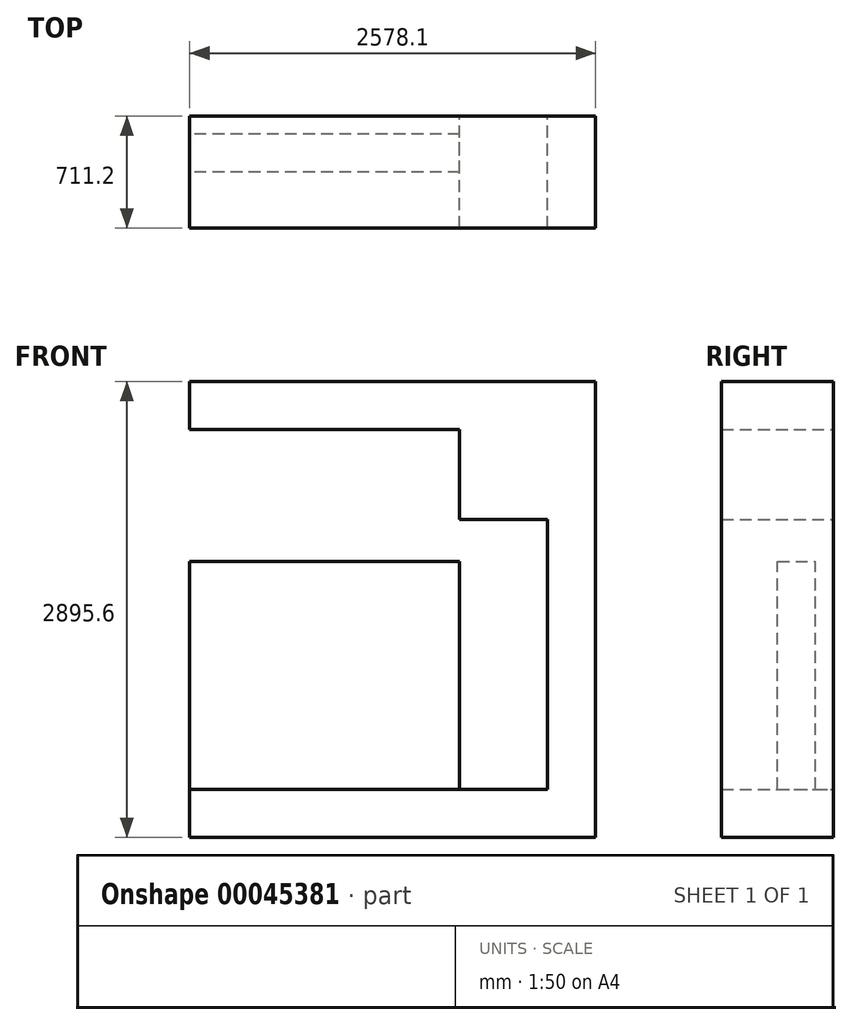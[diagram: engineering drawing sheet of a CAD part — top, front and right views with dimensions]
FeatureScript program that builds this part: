
annotation { "Feature Type Name" : "Feature", "Feature Type Description" : "" }
export const myFeature = defineFeature(function(context is Context, id is Id, definition is map)
    precondition{}
    {
        {
            var Q0;
            Q0=qCreatedBy(makeId("Front.planeOp"),FACE);
            var sketch = newSketch(context, id + "F0", { "sketchPlane" : qUnion([Q0])});
            skLineSegment(sketch, "E0", {"start": v(1136.65, 0) * mm, "end": v(-1136.65, 0) * mm});
            skPoint(sketch, "E1", {"position": v(0, 0) * mm});
            skLineSegment(sketch, "E2", {"start": v(1136.65, 0) * mm, "end": v(1136.65, 1714.5) * mm});
            skLineSegment(sketch, "E3", {"start": v(577.85, 2286) * mm, "end": v(-1136.65, 2286) * mm});
            skLineSegment(sketch, "E4", {"start": v(577.85, 1714.5) * mm, "end": v(577.85, 2286) * mm});
            skLineSegment(sketch, "E5", {"start": v(577.85, 1714.5) * mm, "end": v(1136.65, 1714.5) * mm});
            skLineSegment(sketch, "E6", {"start": v(-1136.65, 2286) * mm, "end": v(-1136.65, 2590.8) * mm});
            skLineSegment(sketch, "E7", {"start": v(-1136.65, 2590.8) * mm, "end": v(1441.45, 2590.8) * mm});
            skLineSegment(sketch, "E8", {"start": v(1441.45, 2590.8) * mm, "end": v(1441.45, -304.8) * mm});
            skLineSegment(sketch, "E9", {"start": v(1441.45, -304.8) * mm, "end": v(-1136.65, -304.8) * mm});
            skLineSegment(sketch, "E10", {"start": v(-1136.65, -304.8) * mm, "end": v(-1136.65, 0) * mm});
            skSolve(sketch);
        }
        {
            var Q0;
            Q0 = qSketchRegion(id + "F0", true);
            extrude(context, id + "F1", {"entities" : qUnion([Q0]), "endBound" : BoundingType.SYMMETRIC, "depth" : 711.2 * mm});
        }
        {
            var Q0;
            Q0=qCreatedBy(makeId("Front.planeOp"),FACE);
            var sketch = newSketch(context, id + "F2", { "sketchPlane" : qUnion([Q0])});
            skLineSegment(sketch, "E11", {"start": v(-1136.65, 0) * mm, "end": v(-1136.65, 1447.8) * mm});
            skLineSegment(sketch, "E12", {"start": v(-1136.65, 1447.8) * mm, "end": v(577.85, 1447.8) * mm});
            skLineSegment(sketch, "E13.0", {"start": v(577.85, 0) * mm, "end": v(-1136.65, 0) * mm});
            skLineSegment(sketch, "E14", {"start": v(577.85, 1714.5) * mm, "end": v(577.85, 0) * mm, "construction": true});
            skLineSegment(sketch, "E15", {"start": v(577.85, 0) * mm, "end": v(577.85, 1447.8) * mm});
            skSolve(sketch);
        }
        {
            var Q0;
            Q0 = qSketchRegion(id + "F2", true);
            extrude(context, id + "F3", {"entities" : qUnion([Q0]), "depth" : 28 / 50.8 * mm});
        }
        {
            var Q0;
            Q0=makeQuery(id+"F3.opExtrude","CAP_FACE",FACE,{"disambiguationData":[OSD([sQuery(id+"F2.wireOp",EDGE,"E11"),sQuery(id+"F2.wireOp",EDGE,"E12"),sQuery(id+"F2.wireOp",EDGE,"9e4527d2-3db6-427e-b9c4-22552d999ceb.0"),sQuery(id+"F2.wireOp",EDGE,"E13.0")])],"isStart":true});
            var sketch = newSketch(context, id + "F4", { "sketchPlane" : qUnion([Q0])});
            skLineSegment(sketch, "E16.0", {"start": v(1136.65, 1447.8) * mm, "end": v(-577.85, 1447.8) * mm});
            skLineSegment(sketch, "E17.0", {"start": v(1136.65, 0) * mm, "end": v(1136.65, 1447.8) * mm});
            skLineSegment(sketch, "E18.0", {"start": v(-577.85, 0) * mm, "end": v(1136.65, 0) * mm});
            skLineSegment(sketch, "E19", {"start": v(-577.85, 1714.5) * mm, "end": v(-577.85, 1447.8) * mm, "construction": true});
            skLineSegment(sketch, "E20", {"start": v(-577.85, 1447.8) * mm, "end": v(-577.85, 0) * mm});
            skSolve(sketch);
        }
        {
            var Q0;
            Q0 = qSketchRegion(id + "F4", true);
            extrude(context, id + "F5", {"entities" : qUnion([Q0]), "operationType" : NewBodyOperationType.ADD, "depth" : 241.3 * mm});
        }
    });
